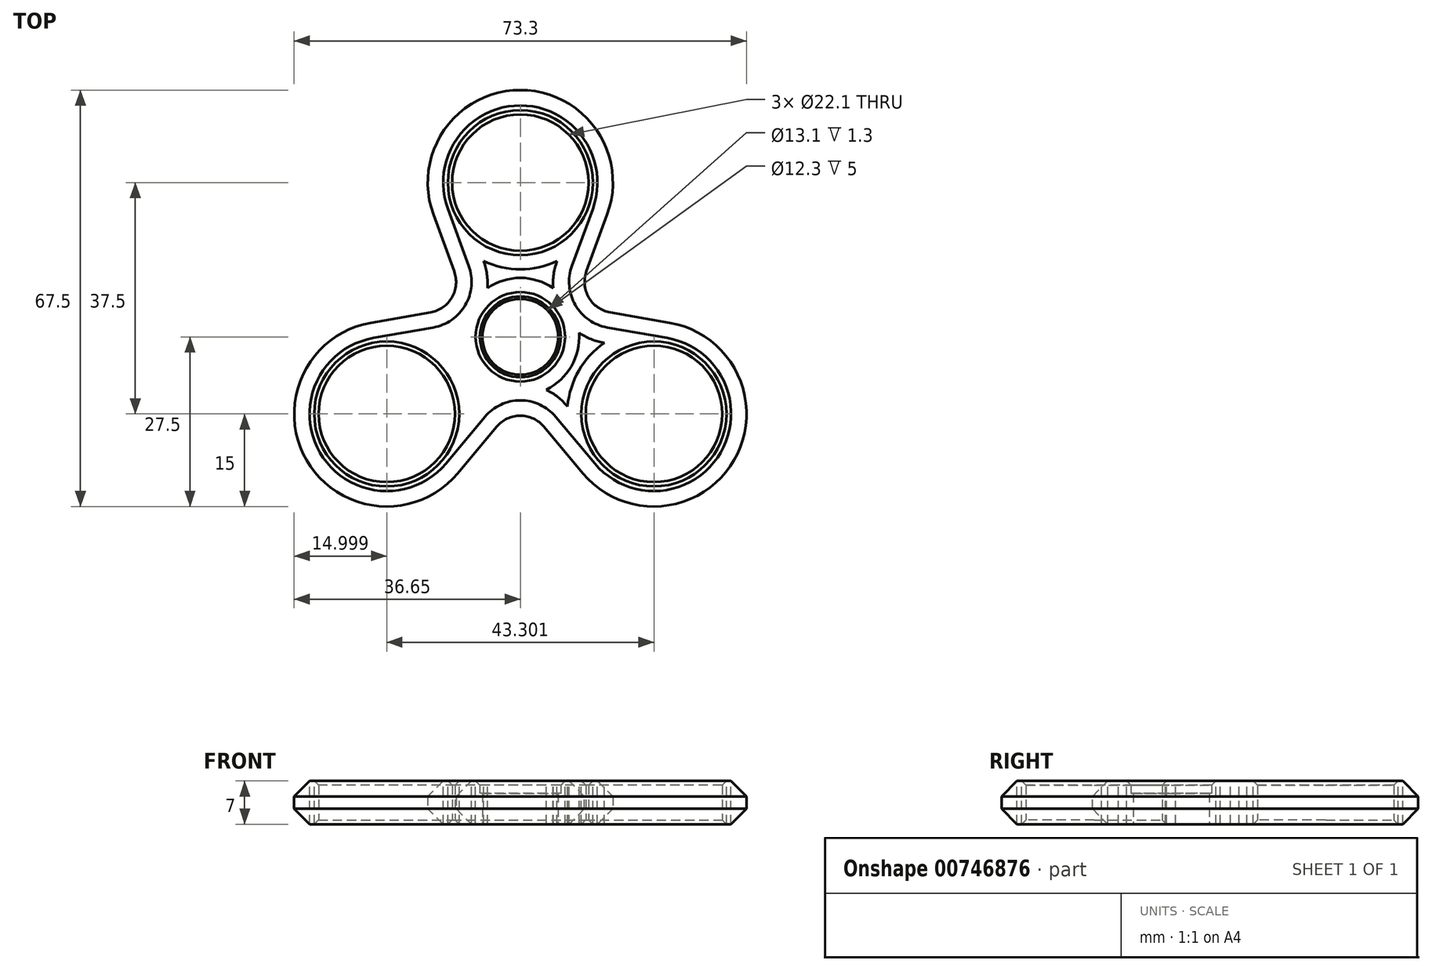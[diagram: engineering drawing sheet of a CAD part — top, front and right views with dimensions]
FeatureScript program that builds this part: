
annotation { "Feature Type Name" : "Feature", "Feature Type Description" : "" }
export const myFeature = defineFeature(function(context is Context, id is Id, definition is map)
    precondition{}
    {
        {
            var Q0;
            Q0=qCreatedBy(makeId("Top.planeOp"),FACE);
            var sketch = newSketch(context, id + "F0", { "sketchPlane" : qUnion([Q0])});
            skLineSegment(sketch, "E0", {"start": v(0, 0) * mm, "end": v(0, 25) * mm, "construction": true});
            skCircle(sketch, "E1", {"center": v(0, 25) * mm, "radius": 11.05 * mm});
            skArc(sketch, "E2", {"start": v(14.09, 19.85) * mm, "mid": v(0, 40) * mm, "end": v(-14.09, 19.85) * mm});
            skCircle(sketch, "E3", {"center": v(0, 0) * mm, "radius": 6.55 * mm});
            skArc(sketch, "E4.1.2", {"start": v(-24.24, 2.28) * mm, "mid": v(-34.64, -20) * mm, "end": v(-10.15, -22.13) * mm});
            skCircle(sketch, "E4.1.3", {"center": v(-21.65, -12.5) * mm, "radius": 11.05 * mm});
            skArc(sketch, "E4.2.2", {"start": v(10.15, -22.13) * mm, "mid": v(34.64, -20) * mm, "end": v(24.24, 2.28) * mm});
            skCircle(sketch, "E4.2.3", {"center": v(21.65, -12.5) * mm, "radius": 11.05 * mm});
            skLineSegment(sketch, "E5", {"start": v(0, 0) * mm, "end": v(-21.65, -12.5) * mm, "construction": true});
            skLineSegment(sketch, "E6", {"start": v(0, 0) * mm, "end": v(21.65, -12.5) * mm, "construction": true});
            skCircle(sketch, "E7", {"center": v(0, 0) * mm, "radius": 10 * mm, "construction": true});
            skLineSegment(sketch, "E8", {"start": v(0, 0) * mm, "end": v(-18.49, 10.67) * mm, "construction": true});
            skLineSegment(sketch, "E9", {"start": v(0, 0) * mm, "end": v(19.4, 11.2) * mm, "construction": true});
            skLineSegment(sketch, "E10", {"start": v(0, 0) * mm, "end": v(0, -30.9) * mm, "construction": true});
            skLineSegment(sketch, "E11", {"start": v(0, -10) * mm, "end": v(10.15, -22.13) * mm});
            skLineSegment(sketch, "E12", {"start": v(-14.09, 19.85) * mm, "end": v(-8.66, 5) * mm});
            skLineSegment(sketch, "E13", {"start": v(14.09, 19.85) * mm, "end": v(8.66, 5) * mm});
            skLineSegment(sketch, "E14", {"start": v(8.66, 5) * mm, "end": v(24.24, 2.28) * mm});
            skLineSegment(sketch, "E15", {"start": v(-24.24, 2.28) * mm, "end": v(-8.66, 5) * mm});
            skLineSegment(sketch, "E16", {"start": v(-10.15, -22.13) * mm, "end": v(0, -10) * mm});
            skSolve(sketch);
        }
        {
            var Q0;
            Q0=qSketchRegion(id+"F0",true);
            extrude(context, id + "F1", {"entities" : qUnion([Q0]), "depth" : 7 * mm, "offsetDistance" : 25 * mm});
        }
        {
            var Q0;
            Q0=makeQuery(id+"F1.opExtrude","SWEPT_EDGE",EDGE,{"disambiguationData":[OSD([sQuery(id+"F0.wireOp",EDGE,"hYaDFHxH-SQ1h-cJ0F-NxPf-ypNw5k6PqgM9"),sQuery(id+"F0.wireOp",EDGE,"E4.1.2")])]});
            var Q1;
            Q1=makeQuery(id+"F1.opExtrude","SWEPT_EDGE",EDGE,{"disambiguationData":[OSD([sQuery(id+"F0.wireOp",EDGE,"hYaDFHxH-SQ1h-cJ0F-NxPf-ypNw5k6PqgM9"),sQuery(id+"F0.wireOp",EDGE,"E4.2.2")])]});
            var Q2;
            Q2=makeQuery(id+"F1.opExtrude","SWEPT_EDGE",EDGE,{"disambiguationData":[OSD([sQuery(id+"F0.wireOp",EDGE,"E4.2.2"),sQuery(id+"F0.wireOp",EDGE,"79da703c-30cb-4167-bd47-66bc16433dd5.trimOffspring")])]});
            var Q3;
            Q3=makeQuery(id+"F1.opExtrude","SWEPT_EDGE",EDGE,{"disambiguationData":[OSD([sQuery(id+"F0.wireOp",EDGE,"E2"),sQuery(id+"F0.wireOp",EDGE,"79da703c-30cb-4167-bd47-66bc16433dd5.trimOffspring")])]});
            var Q4;
            Q4=makeQuery(id+"F1.opExtrude","SWEPT_EDGE",EDGE,{"disambiguationData":[OSD([sQuery(id+"F0.wireOp",EDGE,"E2"),sQuery(id+"F0.wireOp",EDGE,"007a9c35-0cf0-4482-a21c-6fcd3d696d74.trimOffspring")])]});
            var Q5;
            Q5=makeQuery(id+"F1.opExtrude","SWEPT_EDGE",EDGE,{"disambiguationData":[OSD([sQuery(id+"F0.wireOp",EDGE,"E4.1.2"),sQuery(id+"F0.wireOp",EDGE,"007a9c35-0cf0-4482-a21c-6fcd3d696d74.trimOffspring")])]});
            var Q6;
            Q6=makeQuery(id+"F1.opExtrude","SWEPT_EDGE",EDGE,{"disambiguationData":[OSD([sQuery(id+"F0.wireOp",EDGE,"ko7YyKQN-v9HZ-TaP5-rlhh-JDPldfvfd3NA"),sQuery(id+"F0.wireOp",EDGE,"E11")])]});
            var Q7;
            Q7=makeQuery(id+"F1.opExtrude","SWEPT_EDGE",EDGE,{"disambiguationData":[OSD([sQuery(id+"F0.wireOp",EDGE,"E13"),sQuery(id+"F0.wireOp",EDGE,"ksaeEowJ-kkjK-LKTK-lz2Y-0PddznCG0J7x")])]});
            var Q8;
            Q8=makeQuery(id+"F1.opExtrude","SWEPT_EDGE",EDGE,{"disambiguationData":[OSD([sQuery(id+"F0.wireOp",EDGE,"E12"),sQuery(id+"F0.wireOp",EDGE,"UxPp5yaT-IkeL-iCmG-1cEm-yVI7vS4TBKel")])]});
            fillet(context, id + "F2", {"entities" : qUnion([Q0, Q1, Q2, Q3, Q4, Q5, Q6, Q7, Q8]), "radius" : 5 * mm, "tangentPropagation" : true, "allowEdgeOverflow" : false});
        }
        {
            var Q0;
            Q0=makeQuery(id+"F1.opExtrude","CAP_EDGE",EDGE,{"disambiguationData":[OSD([sQuery(id+"F0.wireOp",EDGE,"E15")])],"isStart":false});
            var Q1;
            Q1=makeQuery(id+"F1.opExtrude","CAP_EDGE",EDGE,{"disambiguationData":[OSD([sQuery(id+"F0.wireOp",EDGE,"E16")])],"isStart":true});
            chamfer(context, id + "F3", {"entities" : qUnion([Q0, Q1]), "width" : 2.5 * mm, "tangentPropagation" : true});
        }
        {
            var Q0;
            Q0=makeQuery(id+"F1.opExtrude","CAP_FACE",FACE,{"disambiguationData":[OSD([sQuery(id+"F0.wireOp",EDGE,"E1"),sQuery(id+"F0.wireOp",EDGE,"E2"),sQuery(id+"F0.wireOp",EDGE,"E3"),sQuery(id+"F0.wireOp",EDGE,"E4.1.2"),sQuery(id+"F0.wireOp",EDGE,"E4.1.3"),sQuery(id+"F0.wireOp",EDGE,"E4.2.2"),sQuery(id+"F0.wireOp",EDGE,"E4.2.3"),sQuery(id+"F0.wireOp",EDGE,"E11"),sQuery(id+"F0.wireOp",EDGE,"E12"),sQuery(id+"F0.wireOp",EDGE,"E13"),sQuery(id+"F0.wireOp",EDGE,"E14"),sQuery(id+"F0.wireOp",EDGE,"E15"),sQuery(id+"F0.wireOp",EDGE,"E16")])],"isStart":true});
            var sketch = newSketch(context, id + "F4", { "sketchPlane" : qUnion([Q0])});
            skCircle(sketch, "E17.0", {"center": v(0, 0) * mm, "radius": 6.55 * mm});
            skCircle(sketch, "E18", {"center": v(0, 0) * mm, "radius": 6.15 * mm});
            skSolve(sketch);
        }
        {
            var Q0;
            Q0=qSketchRegion(id+"F4",true);
            extrude(context, id + "F5", {"entities" : qUnion([Q0]), "operationType" : NewBodyOperationType.ADD, "oppositeDirection" : true, "depth" : 5 * mm, "offsetDistance" : 25 * mm});
        }
        {
            var Q0;
            Q0=makeQuery(id+"F1.opExtrude","CAP_EDGE",EDGE,{"disambiguationData":[OSD([sQuery(id+"F0.wireOp",EDGE,"E3")])],"isStart":false});
            var Q1;
            Q1=makeQuery(id+"F1.opExtrude","CAP_EDGE",EDGE,{"disambiguationData":[OSD([sQuery(id+"F0.wireOp",EDGE,"E4.1.3")])],"isStart":false});
            var Q2;
            Q2=makeQuery(id+"F1.opExtrude","CAP_EDGE",EDGE,{"disambiguationData":[OSD([sQuery(id+"F0.wireOp",EDGE,"E4.2.3")])],"isStart":false});
            var Q3;
            Q3=makeQuery(id+"F1.opExtrude","CAP_EDGE",EDGE,{"disambiguationData":[OSD([sQuery(id+"F0.wireOp",EDGE,"E1")])],"isStart":false});
            var Q4;
            Q4=makeQuery(id+"F1.opExtrude","CAP_EDGE",EDGE,{"disambiguationData":[OSD([sQuery(id+"F0.wireOp",EDGE,"E4.1.3")])],"isStart":true});
            var Q5;
            Q5=makeQuery(id+"F1.opExtrude","CAP_EDGE",EDGE,{"disambiguationData":[OSD([sQuery(id+"F0.wireOp",EDGE,"E4.2.3")])],"isStart":true});
            var Q6;
            Q6=makeQuery(id+"F1.opExtrude","CAP_EDGE",EDGE,{"disambiguationData":[OSD([sQuery(id+"F0.wireOp",EDGE,"E1")])],"isStart":true});
            chamfer(context, id + "F6", {"entities" : qUnion([Q0, Q1, Q2, Q3, Q4, Q5, Q6]), "width" : .7 * mm, "tangentPropagation" : true});
        }
        {
            var Q0;
            Q0=makeQuery(id+"F1.opExtrude","CAP_FACE",FACE,{"disambiguationData":[OSD([sQuery(id+"F0.wireOp",EDGE,"E1"),sQuery(id+"F0.wireOp",EDGE,"E3"),sQuery(id+"F0.wireOp",EDGE,"E4.1.3"),sQuery(id+"F0.wireOp",EDGE,"E4.2.3"),sQuery(id+"F0.wireOp",EDGE,"E11"),sQuery(id+"F0.wireOp",EDGE,"E12"),sQuery(id+"F0.wireOp",EDGE,"E13"),sQuery(id+"F0.wireOp",EDGE,"E14"),sQuery(id+"F0.wireOp",EDGE,"E15"),sQuery(id+"F0.wireOp",EDGE,"E16"),sQuery(id+"F0.wireOp",EDGE,"E2"),sQuery(id+"F0.wireOp",EDGE,"E4.2.2"),sQuery(id+"F0.wireOp",EDGE,"E4.1.2")])],"isStart":false});
            var sketch = newSketch(context, id + "F7", { "sketchPlane" : qUnion([Q0])});
            skArc(sketch, "E19.0", {"start": v(-5.75, -12.98) * mm, "mid": v(0, -10.3) * mm, "end": v(5.75, -12.98) * mm, "construction": true});
            skArc(sketch, "E19.2", {"start": v(14.12, 1.5) * mm, "mid": v(8.91, 5.15) * mm, "end": v(8.36, 11.47) * mm, "construction": true});
            skArc(sketch, "E20", {"start": v(-9.53, 0.66) * mm, "mid": v(-8.27, -4.77) * mm, "end": v(-4.2, -8.58) * mm});
            skArc(sketch, "E21", {"start": v(-7.65, -11.3) * mm, "mid": v(-9.48, -5.47) * mm, "end": v(-13.6, -0.98) * mm});
            skArc(sketch, "E22.1", {"start": v(-9.53, 0.66) * mm, "mid": v(-11.48, -0.38) * mm, "end": v(-13.6, -0.98) * mm});
            skLineSegment(sketch, "E23", {"start": v(0, 0) * mm, "end": v(-21.65, -12.5) * mm, "construction": true});
            skLineSegment(sketch, "E24", {"start": v(0, 0) * mm, "end": v(-15.32, 9.18) * mm, "construction": true});
            skArc(sketch, "E25.MirrorCS", {"start": v(-4.2, -8.58) * mm, "mid": v(-6.07, -9.75) * mm, "end": v(-7.65, -11.3) * mm});
            skArc(sketch, "E26.1.0", {"start": v(4.2, -8.58) * mm, "mid": v(6.07, -9.75) * mm, "end": v(7.65, -11.3) * mm});
            skArc(sketch, "E26.1.1", {"start": v(13.6, -0.98) * mm, "mid": v(9.48, -5.48) * mm, "end": v(7.65, -11.3) * mm});
            skArc(sketch, "E26.1.2", {"start": v(4.2, -8.58) * mm, "mid": v(8.27, -4.78) * mm, "end": v(9.53, 0.66) * mm});
            skArc(sketch, "E26.1.3", {"start": v(9.53, 0.66) * mm, "mid": v(11.48, -0.38) * mm, "end": v(13.6, -0.98) * mm});
            skArc(sketch, "E26.2.0", {"start": v(5.33, 7.92) * mm, "mid": v(5.4, 10.13) * mm, "end": v(5.95, 12.27) * mm});
            skArc(sketch, "E26.2.1", {"start": v(-5.95, 12.27) * mm, "mid": v(0, 10.95) * mm, "end": v(5.95, 12.27) * mm});
            skArc(sketch, "E26.2.2", {"start": v(5.33, 7.92) * mm, "mid": v(0, 9.55) * mm, "end": v(-5.33, 7.92) * mm});
            skArc(sketch, "E26.2.3", {"start": v(-5.33, 7.92) * mm, "mid": v(-5.4, 10.13) * mm, "end": v(-5.95, 12.27) * mm});
            skSolve(sketch);
        }
        {
            var Q0;
            Q0=makeQuery(id+"F7.imprint","IMPRINT",FACE,{"disambiguationData":[TD([[makeQuery(id+"F7.imprint","IMPRINT",EDGE,{"derivedFrom":sQuery(id+"F7.wireOp",EDGE,"E20")}),-1.0]])]});
            var Q1;
            Q1=makeQuery(id+"F7.imprint","IMPRINT",FACE,{"disambiguationData":[TD([[makeQuery(id+"F7.imprint","IMPRINT",EDGE,{"derivedFrom":sQuery(id+"F7.wireOp",EDGE,"E26.2.0")}),1.0]])]});
            var Q2;
            Q2=makeQuery(id+"F7.imprint","IMPRINT",FACE,{"disambiguationData":[TD([[makeQuery(id+"F7.imprint","IMPRINT",EDGE,{"derivedFrom":sQuery(id+"F7.wireOp",EDGE,"E26.1.0")}),1.0]])]});
            extrude(context, id + "F8", {"entities" : qUnion([Q0, Q1, Q2]), "operationType" : NewBodyOperationType.REMOVE, "oppositeDirection" : true, "depth" : 25 * mm, "offsetDistance" : 25 * mm});
        }
    });
